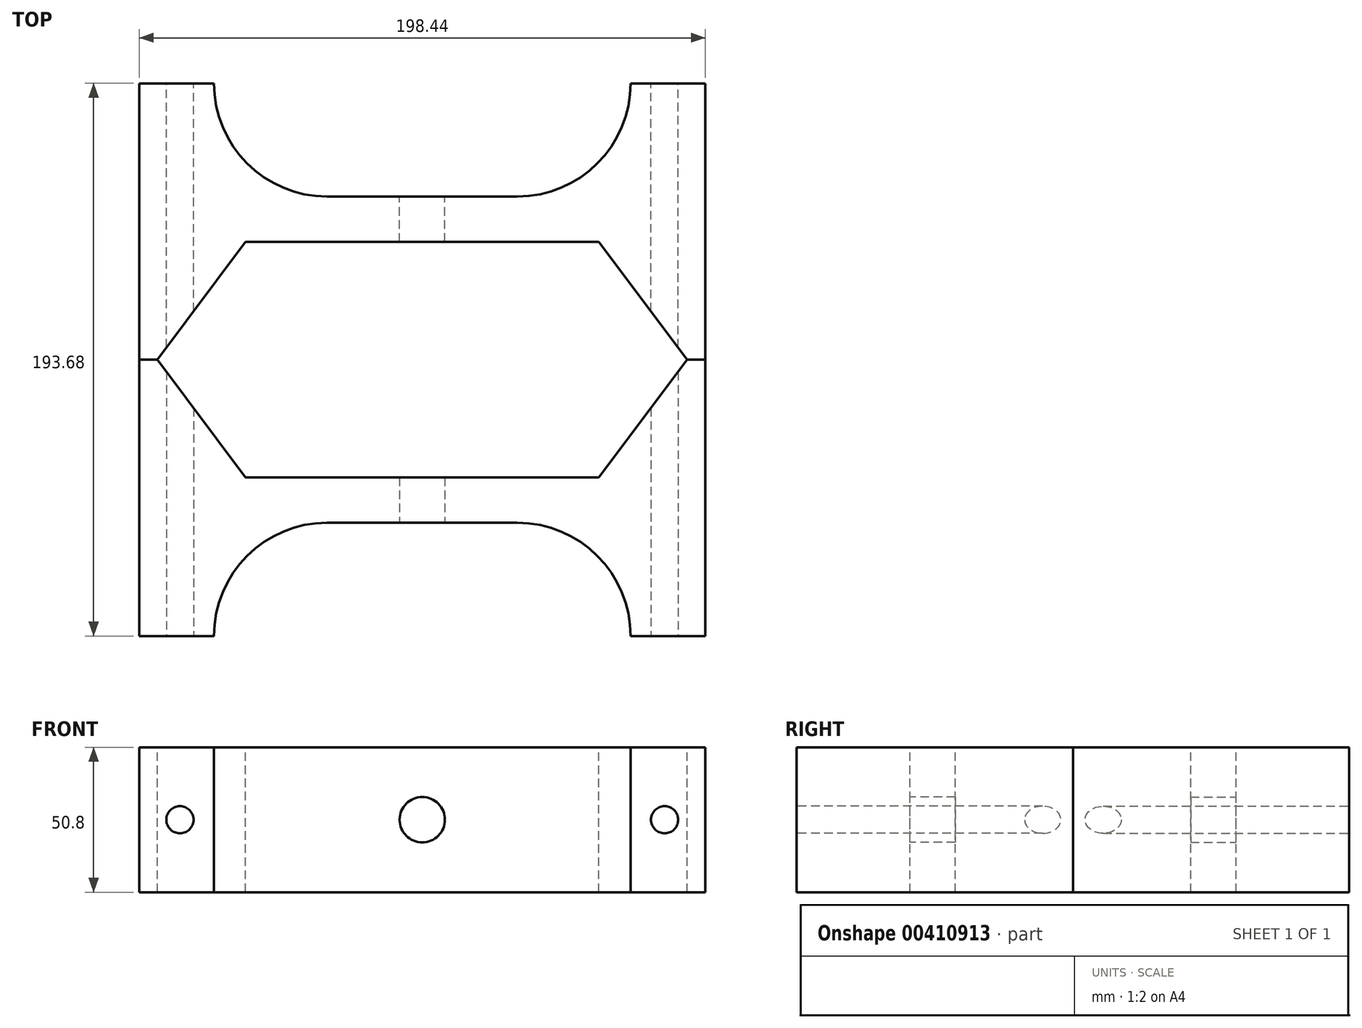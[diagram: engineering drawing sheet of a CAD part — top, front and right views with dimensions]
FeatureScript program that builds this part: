
annotation { "Feature Type Name" : "Feature", "Feature Type Description" : "" }
export const myFeature = defineFeature(function(context is Context, id is Id, definition is map)
    precondition{}
    {
        {
            var Q0;
            Q0=qCreatedBy(makeId("Front.planeOp"),FACE);
            var sketch = newSketch(context, id + "F0", { "sketchPlane" : qUnion([Q0])});
            skLineSegment(sketch, "E0", {"start": v(0, 0) * mm, "end": v(-198.44, 0) * mm});
            skLineSegment(sketch, "E1", {"start": v(-198.44, 0) * mm, "end": v(-198.44, 50.8) * mm});
            skLineSegment(sketch, "E2", {"start": v(-198.44, 50.8) * mm, "end": v(0, 50.8) * mm});
            skLineSegment(sketch, "E3", {"start": v(0, 50.8) * mm, "end": v(0, 0) * mm});
            skSolve(sketch);
        }
        {
            var Q0;
            Q0=makeQuery(id+"F0.imprint","IMPRINT",FACE,{"disambiguationData":[TD([[makeQuery(id+"F0.imprint","IMPRINT",EDGE,{"derivedFrom":sQuery(id+"F0.wireOp",EDGE,"E0")}),-1.0]])]});
            extrude(context, id + "F1", {"entities" : qUnion([Q0]), "depth" : 96.84 * mm});
        }
        {
            var Q0;
            Q0=makeQuery(id+"F1.opExtrude","SWEPT_FACE",FACE,{"disambiguationData":[OSD([sQuery(id+"F0.wireOp",EDGE,"E2")])]});
            var sketch = newSketch(context, id + "F2", { "sketchPlane" : qUnion([Q0])});
            skLineSegment(sketch, "E4", {"start": v(-99.22, -96.84) * mm, "end": v(-172.24, -96.84) * mm});
            skLineSegment(sketch, "E5", {"start": v(-99.22, -96.84) * mm, "end": v(-26.2, -96.84) * mm});
            skLineSegment(sketch, "E6", {"start": v(-172.24, -96.84) * mm, "end": v(-172.24, -57.15) * mm});
            skLineSegment(sketch, "E7", {"start": v(-172.24, -57.15) * mm, "end": v(-26.2, -57.15) * mm});
            skLineSegment(sketch, "E8", {"start": v(-26.2, -57.15) * mm, "end": v(-26.2, -96.84) * mm});
            skLineSegment(sketch, "E9", {"start": v(-172.24, -96.84) * mm, "end": v(-132.56, -96.84) * mm});
            skLineSegment(sketch, "E10", {"start": v(-26.2, -96.84) * mm, "end": v(-65.88, -96.84) * mm});
            skArc(sketch, "E11", {"start": v(-26.2, -96.84) * mm, "mid": v(-37.82, -68.77) * mm, "end": v(-65.88, -57.15) * mm});
            skArc(sketch, "E12", {"start": v(-132.56, -57.15) * mm, "mid": v(-160.62, -68.77) * mm, "end": v(-172.24, -96.84) * mm});
            skPoint(sketch, "E13.endSnap0", {"position": v(-99.22, 0) * mm});
            skLineSegment(sketch, "E14", {"start": v(-99.22, -41.28) * mm, "end": v(-161.13, -41.28) * mm});
            skLineSegment(sketch, "E15", {"start": v(-161.13, -41.28) * mm, "end": v(-192.09, 0) * mm});
            skLineSegment(sketch, "E16", {"start": v(-99.22, -41.28) * mm, "end": v(-37.3, -41.28) * mm});
            skLineSegment(sketch, "E17", {"start": v(-37.3, -41.28) * mm, "end": v(-6.35, 0) * mm});
            skSolve(sketch);
        }
        {
            var Q0;
            Q0=makeQuery(id+"F2.imprint","IMPRINT",FACE,{"disambiguationData":[TD([[makeQuery(id+"F2.imprint","IMPRINT",EDGE,{"derivedFrom":sQuery(id+"F2.wireOp",EDGE,"E4")}),1.0]])]});
            extrude(context, id + "F3", {"entities" : qUnion([Q0]), "operationType" : NewBodyOperationType.REMOVE, "endBound" : BoundingType.THROUGH_ALL, "oppositeDirection" : true, "depth" : 25.4 * mm});
        }
        {
            var Q0;
            Q0=makeQuery(id+"F2.imprint","IMPRINT",FACE,{"disambiguationData":[TD([[makeQuery(id+"F2.imprint","IMPRINT",EDGE,{"derivedFrom":sQuery(id+"F2.wireOp",EDGE,"E14")}),-1.0]])]});
            var Q1;
            Q1=makeQuery(id+"F2.imprint","IMPRINT",FACE,{"disambiguationData":[TD([[makeQuery(id+"F2.imprint","IMPRINT",EDGE,{"derivedFrom":sQuery(id+"F2.wireOp",EDGE,"E4")}),1.0]])]});
            extrude(context, id + "F4", {"entities" : qUnion([Q0, Q1]), "operationType" : NewBodyOperationType.REMOVE, "endBound" : BoundingType.THROUGH_ALL, "oppositeDirection" : true, "depth" : 25.4 * mm});
        }
        {
            var Q0;
            Q0=makeQuery(id+"F3.boolean.opBoolean","COPY",FACE,{"derivedFrom":makeQuery(id+"F3.opExtrude","SWEPT_FACE",FACE,{"disambiguationData":[OSD([sQuery(id+"F2.wireOp",EDGE,"E7")])]})});
            var sketch = newSketch(context, id + "F5", { "sketchPlane" : qUnion([Q0])});
            skCircle(sketch, "E18", {"center": v(-99.22, 25.4) * mm, "radius": 7.94 * mm});
            skSolve(sketch);
        }
        {
            var Q0;
            Q0=makeQuery(id+"F5.imprint","IMPRINT",FACE,{"disambiguationData":[TD([[makeQuery(id+"F5.imprint","IMPRINT",EDGE,{"derivedFrom":sQuery(id+"F5.wireOp",EDGE,"E18")}),1.0]])]});
            extrude(context, id + "F6", {"entities" : qUnion([Q0]), "operationType" : NewBodyOperationType.REMOVE, "endBound" : BoundingType.THROUGH_ALL, "oppositeDirection" : true, "depth" : 25.4 * mm});
        }
        {
            var Q0;
            {var subQ0=sQuery(id+"F0.wireOp",EDGE,"E0");var subQ1=sQuery(id+"F0.wireOp",EDGE,"E1");var subQ2=sQuery(id+"F0.wireOp",EDGE,"E2");Q0=makeQuery(id+"F3.boolean.opBoolean","SPLIT",FACE,{"disambiguationData":[TD([makeQuery(id+"F1.opExtrude","SWEPT_FACE",FACE,{"disambiguationData":[OSD([subQ1])]})])],"derivedFrom":makeQuery(id+"F1.opExtrude","CAP_FACE",FACE,{"disambiguationData":[OSD([subQ0,subQ1,subQ2,sQuery(id+"F0.wireOp",EDGE,"E3")])],"isStart":false})});}
            var sketch = newSketch(context, id + "F7", { "sketchPlane" : qUnion([Q0])});
            skLineSegment(sketch, "E19", {"start": v(-198.44, 25.4) * mm, "end": v(-184.15, 25.4) * mm});
            skCircle(sketch, "E20", {"center": v(-184.15, 25.4) * mm, "radius": 4.76 * mm});
            skSolve(sketch);
        }
        {
            var Q0;
            Q0 = qSketchRegion(id + "F7", true);
            extrude(context, id + "F8", {"entities" : qUnion([Q0]), "operationType" : NewBodyOperationType.REMOVE, "endBound" : BoundingType.THROUGH_ALL, "oppositeDirection" : true, "depth" : 25.4 * mm});
        }
        {
            var Q0;
            {var subQ0=sQuery(id+"F0.wireOp",EDGE,"E0");var subQ1=sQuery(id+"F0.wireOp",EDGE,"E3");var subQ2=sQuery(id+"F0.wireOp",EDGE,"E2");Q0=makeQuery(id+"F3.boolean.opBoolean","SPLIT",FACE,{"disambiguationData":[TD([makeQuery(id+"F1.opExtrude","SWEPT_FACE",FACE,{"disambiguationData":[OSD([subQ1])]})])],"derivedFrom":makeQuery(id+"F1.opExtrude","CAP_FACE",FACE,{"disambiguationData":[OSD([subQ0,sQuery(id+"F0.wireOp",EDGE,"E1"),subQ2,subQ1])],"isStart":false})});}
            var sketch = newSketch(context, id + "F9", { "sketchPlane" : qUnion([Q0])});
            skLineSegment(sketch, "E21", {"start": v(0, 25.4) * mm, "end": v(-14.29, 25.4) * mm});
            skPoint(sketch, "E21.endSnap0", {"position": v(0, 25.4) * mm});
            skCircle(sketch, "E22", {"center": v(-14.29, 25.4) * mm, "radius": 4.76 * mm});
            skSolve(sketch);
        }
        {
            var Q0;
            Q0 = qSketchRegion(id + "F9", true);
            extrude(context, id + "F10", {"entities" : qUnion([Q0]), "operationType" : NewBodyOperationType.REMOVE, "endBound" : BoundingType.THROUGH_ALL, "oppositeDirection" : true, "depth" : 25.4 * mm});
        }
        {
            var Q0;
            Q0=makeQuery(id+"F1.opExtrude","SWEPT_BODY",BODY,{"disambiguationData":[OSD([sQuery(id+"F0.wireOp",EDGE,"E0"),sQuery(id+"F0.wireOp",EDGE,"E1"),sQuery(id+"F0.wireOp",EDGE,"E2"),sQuery(id+"F0.wireOp",EDGE,"E3")])]});
            var Q1;
            Q1=qCreatedBy(makeId("Front.planeOp"),FACE);
            mirror(context, id + "F11", {"entities" : qUnion([Q0]), "mirrorPlane" : qUnion([Q1])});
        }
    });
